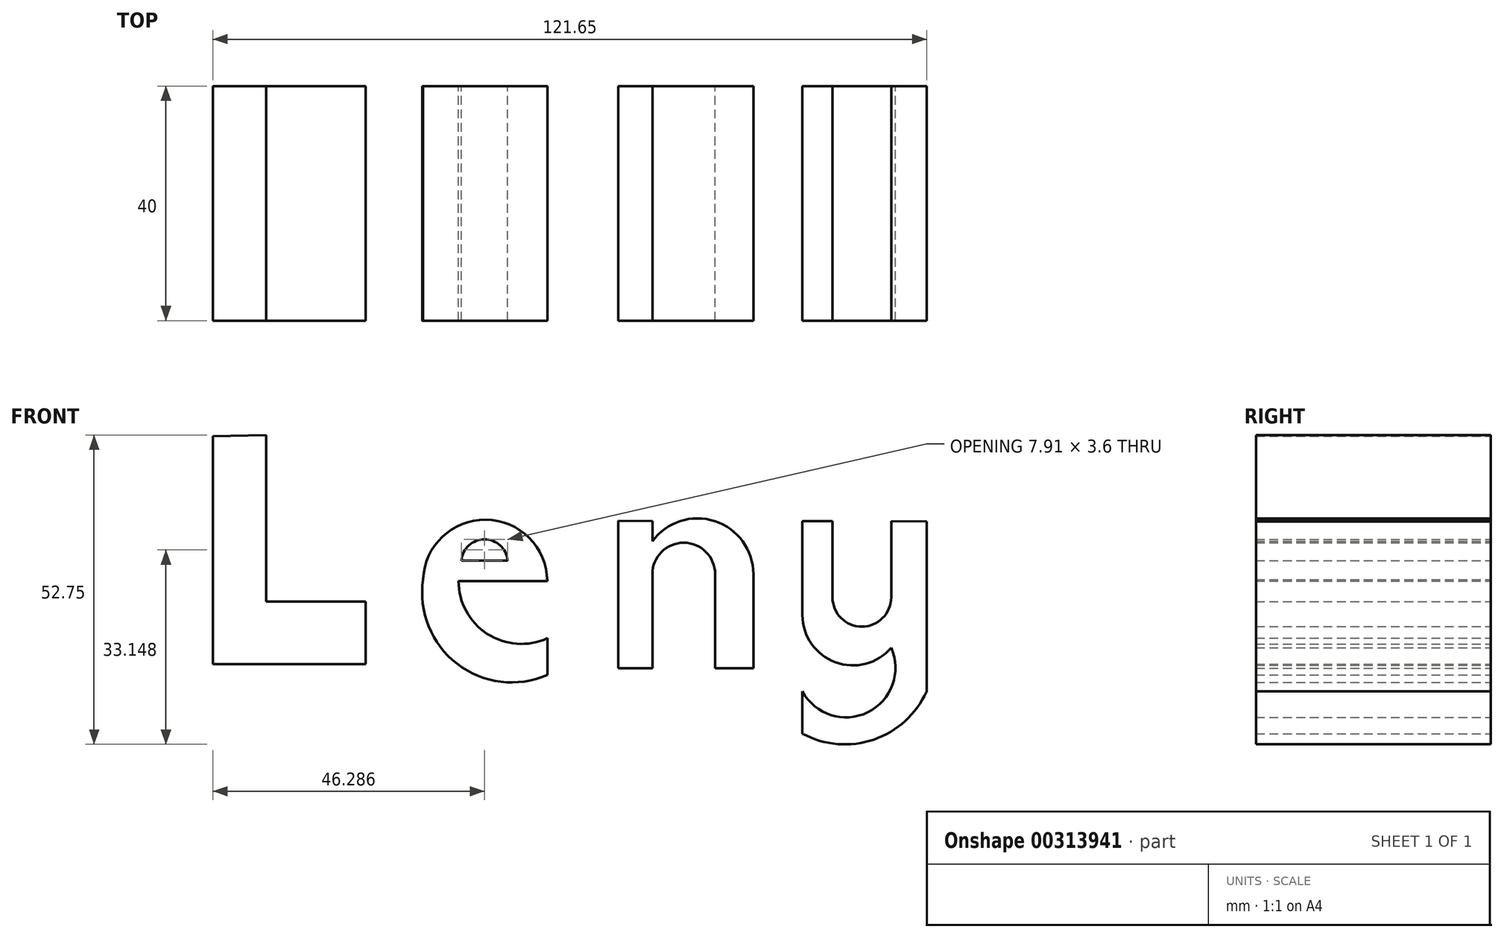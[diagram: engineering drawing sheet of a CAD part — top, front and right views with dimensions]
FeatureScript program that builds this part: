
annotation { "Feature Type Name" : "Feature", "Feature Type Description" : "" }
export const myFeature = defineFeature(function(context is Context, id is Id, definition is map)
    precondition{}
    {
        {
            var Q0;
            Q0=qCreatedBy(makeId("Front.planeOp"),FACE);
            var sketch = newSketch(context, id + "F0", { "sketchPlane" : qUnion([Q0])});
            skLineSegment(sketch, "E0", {"start": v(-69.08, 43.5) * mm, "end": v(-69.08, 4.65) * mm});
            skLineSegment(sketch, "E1", {"start": v(-69.08, 4.65) * mm, "end": v(-43.03, 4.65) * mm});
            skLineSegment(sketch, "E2", {"start": v(-43.03, 4.65) * mm, "end": v(-43.03, 15.35) * mm});
            skLineSegment(sketch, "E3", {"start": v(-43.03, 15.35) * mm, "end": v(-60, 15.35) * mm});
            skLineSegment(sketch, "E4", {"start": v(-60, 15.35) * mm, "end": v(-60, 43.73) * mm});
            skLineSegment(sketch, "E5", {"start": v(-60, 43.73) * mm, "end": v(-69.08, 43.5) * mm});
            skLineSegment(sketch, "E6", {"start": v(-27.21, 18.84) * mm, "end": v(-12.1, 18.84) * mm});
            skLineSegment(sketch, "E7", {"start": v(-12.1, 18.84) * mm, "end": v(-27.21, 18.84) * mm});
            skArc(sketch, "E8", {"start": v(-27.21, 18.84) * mm, "mid": v(-22.32, 9.82) * mm, "end": v(-12.1, 9.07) * mm});
            skLineSegment(sketch, "E9", {"start": v(-12.1, 9.07) * mm, "end": v(-12.1, 2.8) * mm});
            skArc(sketch, "E10", {"start": v(-33.26, 19.07) * mm, "mid": v(-27.46, 4.72) * mm, "end": v(-12.1, 2.8) * mm});
            skArc(sketch, "E11", {"start": v(-12.1, 18.84) * mm, "mid": v(-22.56, 29.3) * mm, "end": v(-33.26, 19.07) * mm});
            skLineSegment(sketch, "E12", {"start": v(-26.75, 22.33) * mm, "end": v(-18.84, 22.33) * mm});
            skArc(sketch, "E13", {"start": v(-18.84, 22.33) * mm, "mid": v(-22.8, 25.93) * mm, "end": v(-26.75, 22.33) * mm});
            skLineSegment(sketch, "E14", {"start": v(0, 29.07) * mm, "end": v(0, 3.95) * mm});
            skLineSegment(sketch, "E15", {"start": v(0, 3.95) * mm, "end": v(5.81, 3.95) * mm});
            skLineSegment(sketch, "E16", {"start": v(5.81, 3.95) * mm, "end": v(5.81, 20) * mm});
            skLineSegment(sketch, "E17", {"start": v(0, 29.07) * mm, "end": v(5.81, 29.02) * mm});
            skLineSegment(sketch, "E18", {"start": v(5.81, 29.02) * mm, "end": v(5.81, 25.58) * mm});
            skLineSegment(sketch, "E19", {"start": v(16.51, 20) * mm, "end": v(16.51, 3.95) * mm});
            skLineSegment(sketch, "E20", {"start": v(16.51, 3.95) * mm, "end": v(23.03, 3.95) * mm});
            skLineSegment(sketch, "E21", {"start": v(23.03, 3.95) * mm, "end": v(23.03, 20) * mm});
            skArc(sketch, "E22", {"start": v(23.03, 20) * mm, "mid": v(16.45, 29.05) * mm, "end": v(5.81, 25.58) * mm});
            skArc(sketch, "E23", {"start": v(16.51, 20) * mm, "mid": v(11.16, 25.35) * mm, "end": v(5.81, 20) * mm});
            skLineSegment(sketch, "E24", {"start": v(31.4, 29.05) * mm, "end": v(36.52, 29.05) * mm});
            skPoint(sketch, "E24.startSnap0", {"position": v(16.45, 29.05) * mm});
            skLineSegment(sketch, "E25", {"start": v(36.52, 29.05) * mm, "end": v(31.4, 29.05) * mm});
            skLineSegment(sketch, "E26", {"start": v(31.4, 13.02) * mm, "end": v(31.4, 29.05) * mm});
            skLineSegment(sketch, "E27", {"start": v(46.52, 29.02) * mm, "end": v(52.57, 29) * mm});
            skLineSegment(sketch, "E28", {"start": v(52.57, 29) * mm, "end": v(52.57, 0) * mm});
            skLineSegment(sketch, "E29", {"start": v(36.52, 29.05) * mm, "end": v(36.52, 16.05) * mm});
            skLineSegment(sketch, "E30", {"start": v(46.52, 29.02) * mm, "end": v(46.52, 16.05) * mm});
            skArc(sketch, "E31", {"start": v(36.52, 16.05) * mm, "mid": v(41.52, 11.05) * mm, "end": v(46.52, 16.05) * mm});
            skArc(sketch, "E32", {"start": v(31.4, 13.02) * mm, "mid": v(37.01, 4.97) * mm, "end": v(46.52, 7.44) * mm});
            skArc(sketch, "E33", {"start": v(31.4, 0) * mm, "mid": v(42.54, -3.55) * mm, "end": v(46.52, 7.44) * mm});
            skLineSegment(sketch, "E34", {"start": v(31.4, 0) * mm, "end": v(31.4, -7.21) * mm});
            skArc(sketch, "E35", {"start": v(31.4, -7.21) * mm, "mid": v(43.55, -8.2) * mm, "end": v(52.57, 0) * mm});
            skSolve(sketch);
        }
        {
            var Q0;
            Q0 = qSketchRegion(id + "F0", true);
            extrude(context, id + "F1", {"entities" : qUnion([Q0]), "depth" : 40 * mm});
        }
    });
